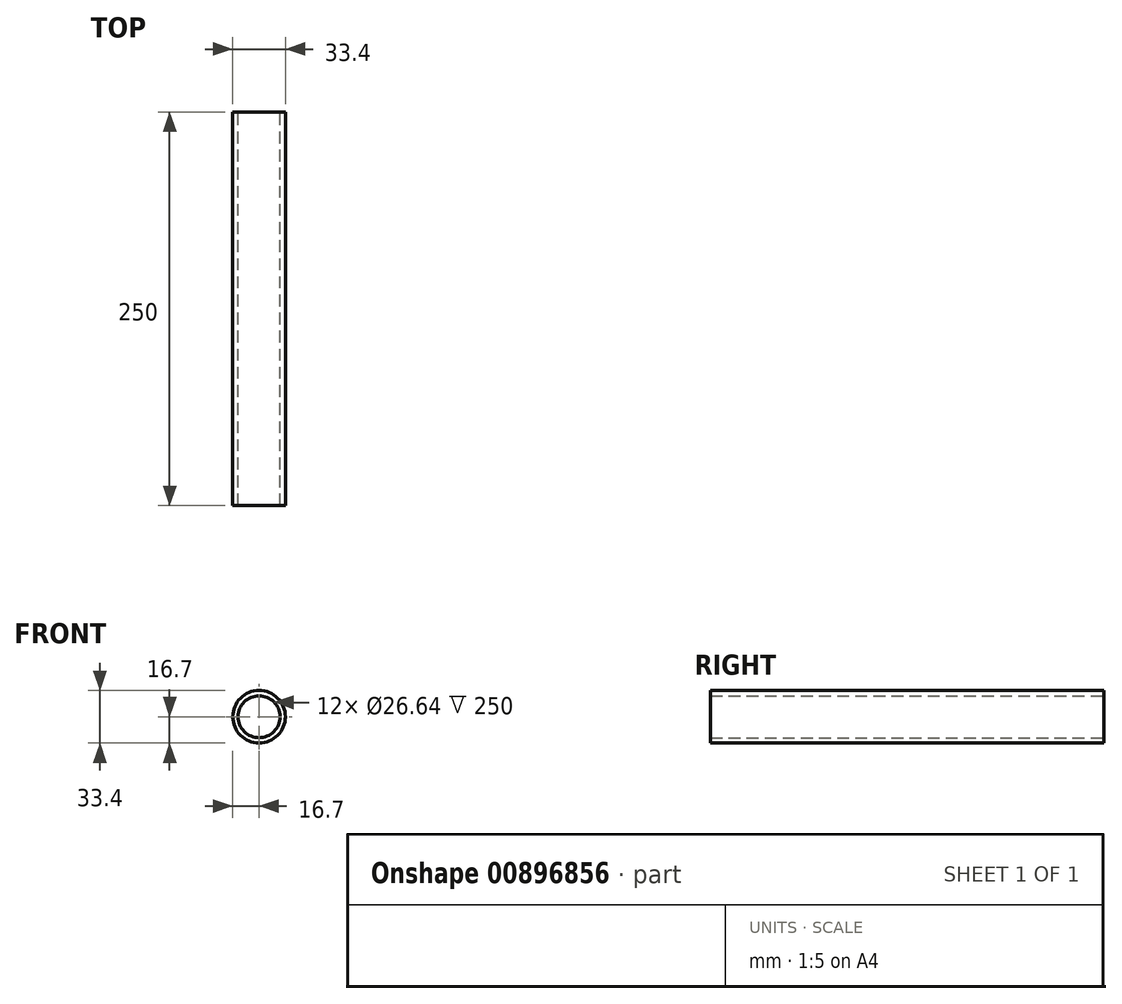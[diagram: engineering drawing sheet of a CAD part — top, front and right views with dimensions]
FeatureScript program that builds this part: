
annotation { "Feature Type Name" : "Feature", "Feature Type Description" : "" }
export const myFeature = defineFeature(function(context is Context, id is Id, definition is map)
    precondition{}
    {
        {
            var Q0;
            Q0=qCreatedBy(makeId("Front.planeOp"),FACE);
            var sketch = newSketch(context, id + "F0", { "sketchPlane" : qUnion([Q0])});
            skCircle(sketch, "E0", {"center": v(0, 0) * mm, "radius": 16.7 * mm});
            skCircle(sketch, "E1", {"center": v(0, 0) * mm, "radius": 13.32 * mm});
            skSolve(sketch);
        }
        {
            var Q0;
            Q0=makeQuery(id+"F0.imprint","IMPRINT",FACE,{"disambiguationData":[TD([[makeQuery(id+"F0.imprint","IMPRINT",EDGE,{"derivedFrom":sQuery(id+"F0.wireOp",EDGE,"E0")}),1.0]])]});
            extrude(context, id + "F1", {"entities" : qUnion([Q0]), "depth" : 250 * mm, "offsetDistance" : 25.4 * mm});
        }
    });
